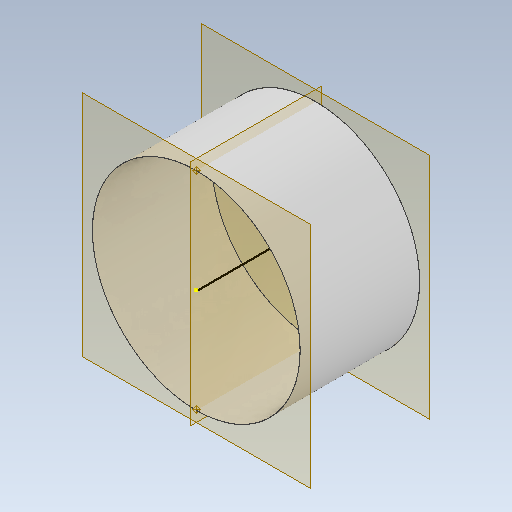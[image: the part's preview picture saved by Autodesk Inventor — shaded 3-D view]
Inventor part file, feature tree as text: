
AUTODESK INVENTOR PART (.ipt)
format: ipt  version: 2021 (Build 250183000, 183)  size: 123,392 bytes
history: native  units: mm
features: other x4, sketch x3, loft x1, shell x1
ambient origin geometry x8: Origin, YZ Plane, XZ Plane, XY Plane, X Axis, Y Axis, Z Axis, Center Point
bodies: Body1 (feature_tree)
feature tree (9):
  other  "Bryła1"
  sketch  "Szkic1"
  other  "Płaszczyzna konstrukcyjna1"
  sketch  "Szkic2"
  sketch  "Szkic 3D2"
  loft  "Wyciągnięcie złożone1"
  shell  "Skorupa1"  Thickness=1000.0mm
  other  "Punkt konstrukcyjny1"
  other  "Punkt konstrukcyjny2"
